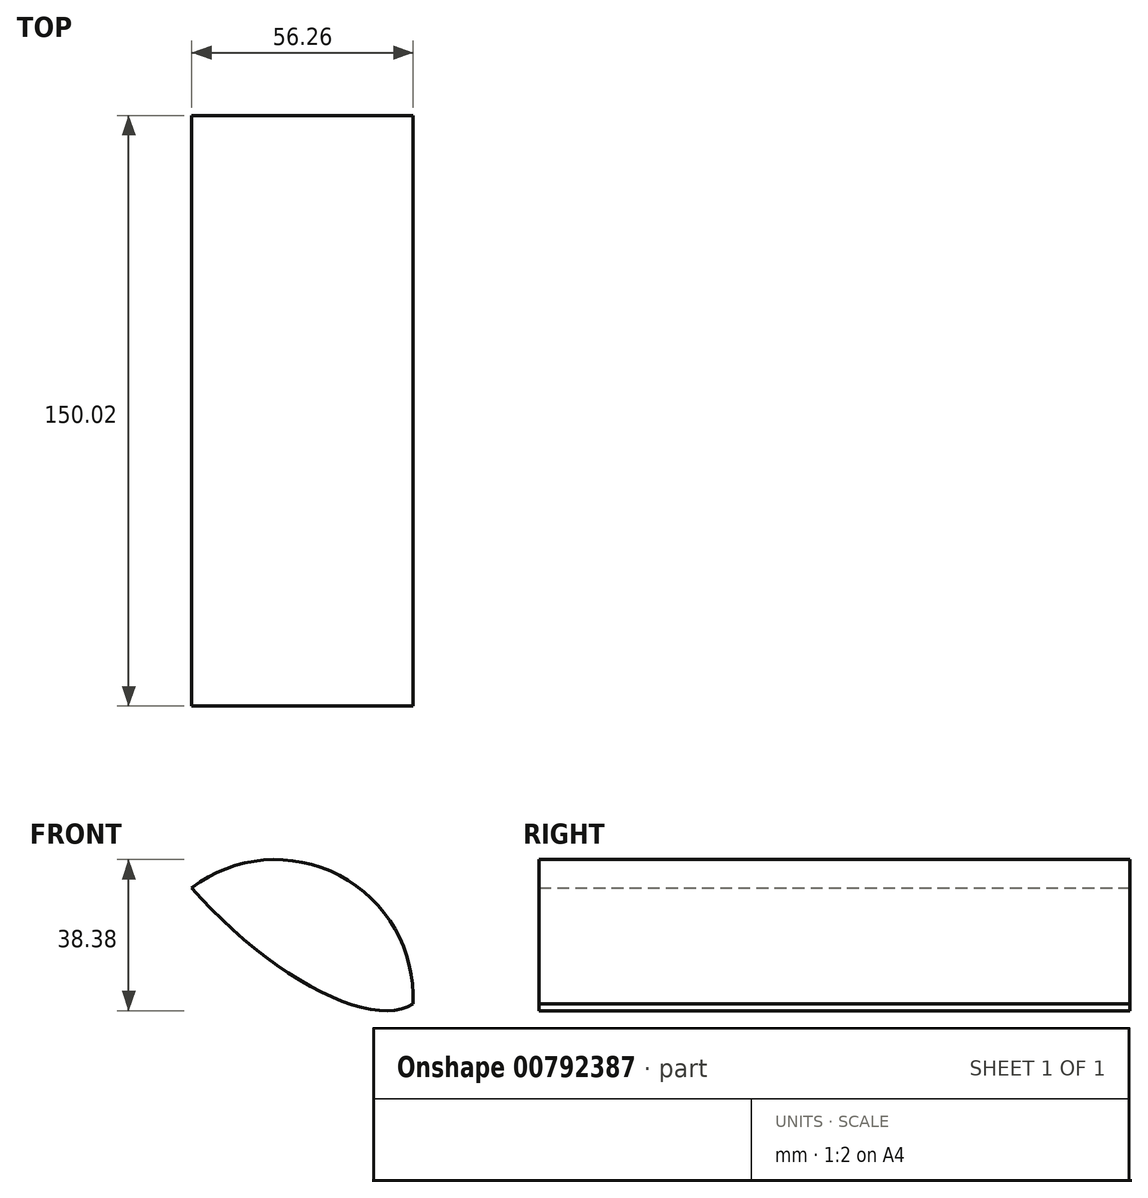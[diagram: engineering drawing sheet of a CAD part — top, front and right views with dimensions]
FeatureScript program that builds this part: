
annotation { "Feature Type Name" : "Feature", "Feature Type Description" : "" }
export const myFeature = defineFeature(function(context is Context, id is Id, definition is map)
    precondition{}
    {
        {
            var Q0;
            Q0=qCreatedBy(makeId("Front.planeOp"),FACE);
            var sketch = newSketch(context, id + "F0", { "sketchPlane" : qUnion([Q0])});
            skLineSegment(sketch, "E0.bottom", {"start": v(-50.87, 47) * mm, "end": v(48, 47) * mm});
            skLineSegment(sketch, "E0.top", {"start": v(-50.87, -53) * mm, "end": v(48, -53) * mm});
            skLineSegment(sketch, "E0.left", {"start": v(-50.87, 47) * mm, "end": v(-50.87, -53) * mm});
            skLineSegment(sketch, "E0.right", {"start": v(48, 47) * mm, "end": v(48, -53) * mm});
            skCircle(sketch, "E1", {"center": v(0, 0) * mm, "radius": 35 * mm});
            skSolve(sketch);
        }
        {
            var Q0;
            Q0=makeQuery(id+"F0.imprint","IMPRINT",FACE,{"disambiguationData":[TD([[makeQuery(id+"F0.imprint","IMPRINT",EDGE,{"derivedFrom":sQuery(id+"F0.wireOp",EDGE,"E1")}),1.0]])]});
            extrude(context, id + "F1", {"entities" : qUnion([Q0]), "depth" : 150.02 * mm, "offsetDistance" : 25 * mm});
        }
        {
            var Q0;
            Q0=qCreatedBy(makeId("Front.planeOp"),FACE);
            var sketch = newSketch(context, id + "F2", { "sketchPlane" : qUnion([Q0])});
            skEllipse(sketch, "E2", {"center": v(0, 35.1) * mm, "majorRadius": 50.9 * mm, "minorRadius": 20.48 * mm, "majorAxis": v(0.72, -0.7)});
            skSolve(sketch);
        }
        {
            var Q0;
            Q0 = qSketchRegion(id + "F2", true);
            extrude(context, id + "F3", {"entities" : qUnion([Q0]), "operationType" : NewBodyOperationType.INTERSECT, "depth" : 159.1 * mm, "offsetDistance" : 25 * mm});
        }
    });
